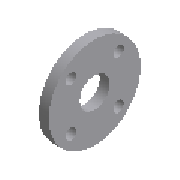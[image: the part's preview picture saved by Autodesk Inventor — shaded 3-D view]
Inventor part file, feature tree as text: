
AUTODESK INVENTOR PART (.ipt)
format: ipt  version: 2025.1 (Build 291241020, 241B)  size: 169,984 bytes
history: native  units: mm (DEFAULTED — no unit token found)
features: other x6, revolve x1, extrude x1, pattern_circular x1
ambient origin geometry x8: Origin, YZ Plane, XZ Plane, XY Plane, X Axis, Y Axis, Z Axis, Center Point
bodies: Solid1 (feature_tree)
feature tree (9):
  other  "DIN 2576 Slip-On Flange for Welding Series 1 (ISO) - PN 10 80 x 88.9"
  revolve  "Revolution1"  Angle=90.0deg
  extrude  "Extrusion1"  Depth=200.0mm
  pattern_circular  "Circular Pattern1"  Count=2  [1 undecoded]
  other  "Work Axis1"
  other  "Work Point1"
  other  "Work Axis2"
  other  "Work Point2"
  other  "Work Point3"
note: 1 required parameter value undecoded (feature->parameter linkage not recoverable at this tier; creation-order binding heuristic only, values carry confidence <= 0.55)
